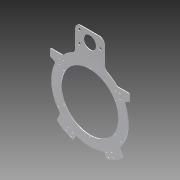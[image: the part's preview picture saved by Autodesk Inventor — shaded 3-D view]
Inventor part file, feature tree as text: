
AUTODESK INVENTOR PART (.ipt)
format: ipt  version: 2014 SP1 (Build 180222100, 222)  size: 308,736 bytes
history: native  units: in
note: dims shown in document units (in); Inventor stores cm internally (conversion verified against a paired STEP export)
features: reference x20, extrude x6, sketch x6, fillet x3, projected_geometry x1
ambient origin geometry x8: Origin, YZ Plane, XZ Plane, XY Plane, X Axis, Y Axis, Z Axis, Center Point
bodies: Solid1 (feature_tree)
feature tree (36):
  extrude  "Extrusion1"  Depth=10.43in
  sketch  "Sketch2"  dims[d2=10.83in d3=0.266in]
  extrude  "Extrusion5"  Depth=0.266in
  extrude  "Extrusion4"  Depth=0.125in TaperAngle=0.0deg
  fillet  "Fillet1"  Radius=0.25in
  fillet  "Fillet2"  Radius=0.375in
  fillet  "Fillet3"  Radius=0.375in
  extrude  "Extrusion6"  Depth=0.25in TaperAngle=0.0deg
  extrude  "Extrusion10"  Depth=0.125in
  extrude  "Extrusion11"  Depth=0.25in
  sketch  "Sketch1"  dims[d0=14.0in d1=10.43in]
  reference  "Reference1"
  reference  "Reference2"
  reference  "Reference3"
  reference  "Reference4"
  reference  "Reference5"
  reference  "Reference6"
  reference  "Reference7"
  reference  "Reference9"
  projected_geometry  "Projected Loop1"
  sketch  "Sketch3"  dims[d4=2.3622in d6=360.0deg d8=0.125in d9=0.0in d11=0.25in d12=0.375in d13=0.375in]
  reference  "Reference10"
  reference  "Reference11"
  sketch  "Sketch4"  dims[d14=0.25in d21=5.0in d22=0.0in]
  reference  "Reference12"
  reference  "Reference13"
  sketch  "Sketch6"  dims[d23=0.125in d24=0.2in]
  reference  "Reference14"
  reference  "Reference15"
  reference  "Reference16"
  reference  "Reference17"
  reference  "Reference18"
  reference  "Reference19"
  sketch  "Sketch7"  dims[d25=0.2in d26=0.25in d27=0.25in d28=0.125in d29=0.0in d30=0.125in d31=0.125in d32=0.125in d33=1.0in d34=0.0in d37=1.05in d50=1.0in d51=1.0in d52=0.75in d53=0.75in d54=0.75in d55=1.0in d56=0.49in d57=0.49in d58=0.49in d63=2.3in d64=0.125in d65=0.0in d66=1.0in d67=0.0in]
  reference  "Reference20"
  reference  "Reference21"
